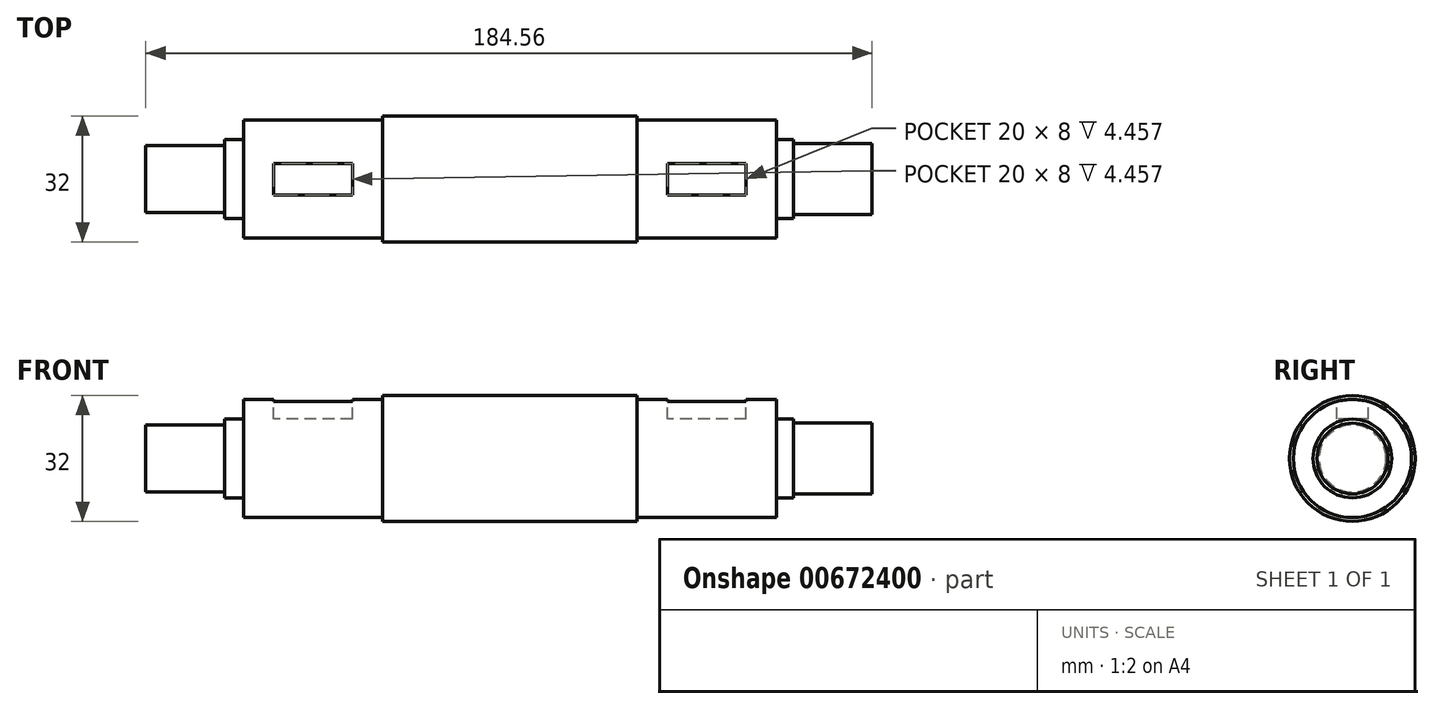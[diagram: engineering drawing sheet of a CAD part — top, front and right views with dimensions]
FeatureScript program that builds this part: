
annotation { "Feature Type Name" : "Feature", "Feature Type Description" : "" }
export const myFeature = defineFeature(function(context is Context, id is Id, definition is map)
    precondition{}
    {
        {
            var Q0;
            Q0=qCreatedBy(makeId("Right.planeOp"),FACE);
            var sketch = newSketch(context, id + "F0", { "sketchPlane" : qUnion([Q0])});
            skCircle(sketch, "E0", {"center": v(0, 0) * mm, "radius": 8.5 * mm});
            skSolve(sketch);
        }
        {
            var Q0;
            Q0 = qSketchRegion(id + "F0", true);
            extrude(context, id + "F1", {"entities" : qUnion([Q0]), "depth" : 20 * mm, "offsetDistance" : 25.4 * mm});
        }
        {
            var Q0;
            Q0=makeQuery(id+"F1.opExtrude","CAP_FACE",FACE,{"disambiguationData":[OSD([sQuery(id+"F0.wireOp",EDGE,"E0")])],"isStart":false});
            var sketch = newSketch(context, id + "F2", { "sketchPlane" : qUnion([Q0])});
            skCircle(sketch, "E1", {"center": v(0, 0) * mm, "radius": 10 * mm});
            skSolve(sketch);
        }
        {
            var Q0;
            Q0 = qSketchRegion(id + "F2", true);
            extrude(context, id + "F3", {"entities" : qUnion([Q0]), "operationType" : NewBodyOperationType.ADD, "depth" : 4.83 * mm, "offsetDistance" : 25.4 * mm});
        }
        {
            var Q0;
            Q0=makeQuery(id+"F3.opExtrude","CAP_FACE",FACE,{"disambiguationData":[OSD([sQuery(id+"F2.wireOp",EDGE,"E1")])],"isStart":false});
            var sketch = newSketch(context, id + "F4", { "sketchPlane" : qUnion([Q0])});
            skCircle(sketch, "E2", {"center": v(0, 0) * mm, "radius": 15 * mm});
            skSolve(sketch);
        }
        {
            var Q0;
            Q0 = qSketchRegion(id + "F4", true);
            extrude(context, id + "F5", {"entities" : qUnion([Q0]), "operationType" : NewBodyOperationType.ADD, "depth" : 35.4 * mm, "offsetDistance" : 25.4 * mm});
        }
        {
            var Q0;
            Q0=makeQuery(id+"F5.opExtrude","CAP_FACE",FACE,{"disambiguationData":[OSD([sQuery(id+"F4.wireOp",EDGE,"E2")])],"isStart":false});
            var sketch = newSketch(context, id + "F6", { "sketchPlane" : qUnion([Q0])});
            skCircle(sketch, "E3", {"center": v(0, 0) * mm, "radius": 16 * mm});
            skSolve(sketch);
        }
        {
            var Q0;
            Q0 = qSketchRegion(id + "F6", true);
            extrude(context, id + "F7", {"entities" : qUnion([Q0]), "operationType" : NewBodyOperationType.ADD, "depth" : 64.6 * mm, "offsetDistance" : 25.4 * mm});
        }
        {
            var Q0;
            Q0=makeQuery(id+"F7.opExtrude","CAP_FACE",FACE,{"disambiguationData":[OSD([sQuery(id+"F6.wireOp",EDGE,"E3")])],"isStart":false});
            var sketch = newSketch(context, id + "F8", { "sketchPlane" : qUnion([Q0])});
            skCircle(sketch, "E4", {"center": v(0, 0) * mm, "radius": 15 * mm});
            skSolve(sketch);
        }
        {
            var Q0;
            Q0 = qSketchRegion(id + "F8", true);
            extrude(context, id + "F9", {"entities" : qUnion([Q0]), "operationType" : NewBodyOperationType.ADD, "depth" : 35.4 * mm, "offsetDistance" : 25.4 * mm});
        }
        {
            var Q0;
            Q0=makeQuery(id+"F9.opExtrude","CAP_FACE",FACE,{"disambiguationData":[OSD([sQuery(id+"F8.wireOp",EDGE,"E4")])],"isStart":false});
            var sketch = newSketch(context, id + "F10", { "sketchPlane" : qUnion([Q0])});
            skCircle(sketch, "E5", {"center": v(0, 0) * mm, "radius": 10 * mm});
            skSolve(sketch);
        }
        {
            var Q0;
            Q0 = qSketchRegion(id + "F10", true);
            extrude(context, id + "F11", {"entities" : qUnion([Q0]), "operationType" : NewBodyOperationType.ADD, "depth" : 4.33 * mm, "offsetDistance" : 25.4 * mm});
        }
        {
            var Q0;
            Q0=makeQuery(id+"F11.opExtrude","CAP_FACE",FACE,{"disambiguationData":[OSD([sQuery(id+"F10.wireOp",EDGE,"E5")])],"isStart":false});
            var sketch = newSketch(context, id + "F12", { "sketchPlane" : qUnion([Q0])});
            skCircle(sketch, "E6", {"center": v(0, 0) * mm, "radius": 9 * mm});
            skSolve(sketch);
        }
        {
            var Q0;
            Q0 = qSketchRegion(id + "F12", true);
            extrude(context, id + "F13", {"entities" : qUnion([Q0]), "operationType" : NewBodyOperationType.ADD, "depth" : 20 * mm, "offsetDistance" : 25.4 * mm});
        }
        {
            var Q0;
            Q0=qCreatedBy(makeId("Top.planeOp"),FACE);
            cPlane(context, id + "F14", {"entities" : qUnion([Q0]), "cplaneType" : CPlaneType.OFFSET, "offset" : 15 * mm, "width" : 152.4 * mm, "height" : 152.4 * mm});
        }
        {
            var Q0;
            Q0=qCreatedBy(id+"F14.planeOp",FACE);
            var sketch = newSketch(context, id + "F15", { "sketchPlane" : qUnion([Q0])});
            skLineSegment(sketch, "E7.0", {"start": v(24.83, 15) * mm, "end": v(24.83, -15) * mm});
            skLineSegment(sketch, "E8.0", {"start": v(60.23, 16) * mm, "end": v(60.23, -16) * mm});
            skLineSegment(sketch, "E9", {"start": v(24.83, 0) * mm, "end": v(60.23, 0) * mm});
            skLineSegment(sketch, "E10.bottom", {"start": v(52.53, 4) * mm, "end": v(32.53, 4) * mm});
            skLineSegment(sketch, "E10.top", {"start": v(52.53, -4) * mm, "end": v(32.53, -4) * mm});
            skLineSegment(sketch, "E10.left", {"start": v(52.53, 4) * mm, "end": v(52.53, -4) * mm});
            skLineSegment(sketch, "E10.right", {"start": v(32.53, 4) * mm, "end": v(32.53, -4) * mm});
            skPoint(sketch, "E10.middle", {"position": v(42.53, 0) * mm});
            skLineSegment(sketch, "E11.0", {"start": v(124.83, 16) * mm, "end": v(124.83, -16) * mm});
            skLineSegment(sketch, "E12.0", {"start": v(160.23, 15) * mm, "end": v(160.23, -15) * mm});
            skLineSegment(sketch, "E13", {"start": v(124.83, 0) * mm, "end": v(160.23, 0) * mm});
            skLineSegment(sketch, "E14.bottom", {"start": v(152.53, 4) * mm, "end": v(132.53, 4) * mm});
            skLineSegment(sketch, "E14.top", {"start": v(152.53, -4) * mm, "end": v(132.53, -4) * mm});
            skLineSegment(sketch, "E14.left", {"start": v(152.53, 4) * mm, "end": v(152.53, -4) * mm});
            skLineSegment(sketch, "E14.right", {"start": v(132.53, 4) * mm, "end": v(132.53, -4) * mm});
            skPoint(sketch, "E14.middle", {"position": v(142.53, 0) * mm});
            skSolve(sketch);
        }
        {
            var Q0;
            Q0 = qSketchRegion(id + "F15", true);
            extrude(context, id + "F16", {"entities" : qUnion([Q0]), "operationType" : NewBodyOperationType.REMOVE, "oppositeDirection" : true, "depth" : 5 * mm, "offsetDistance" : 25.4 * mm});
        }
    });
